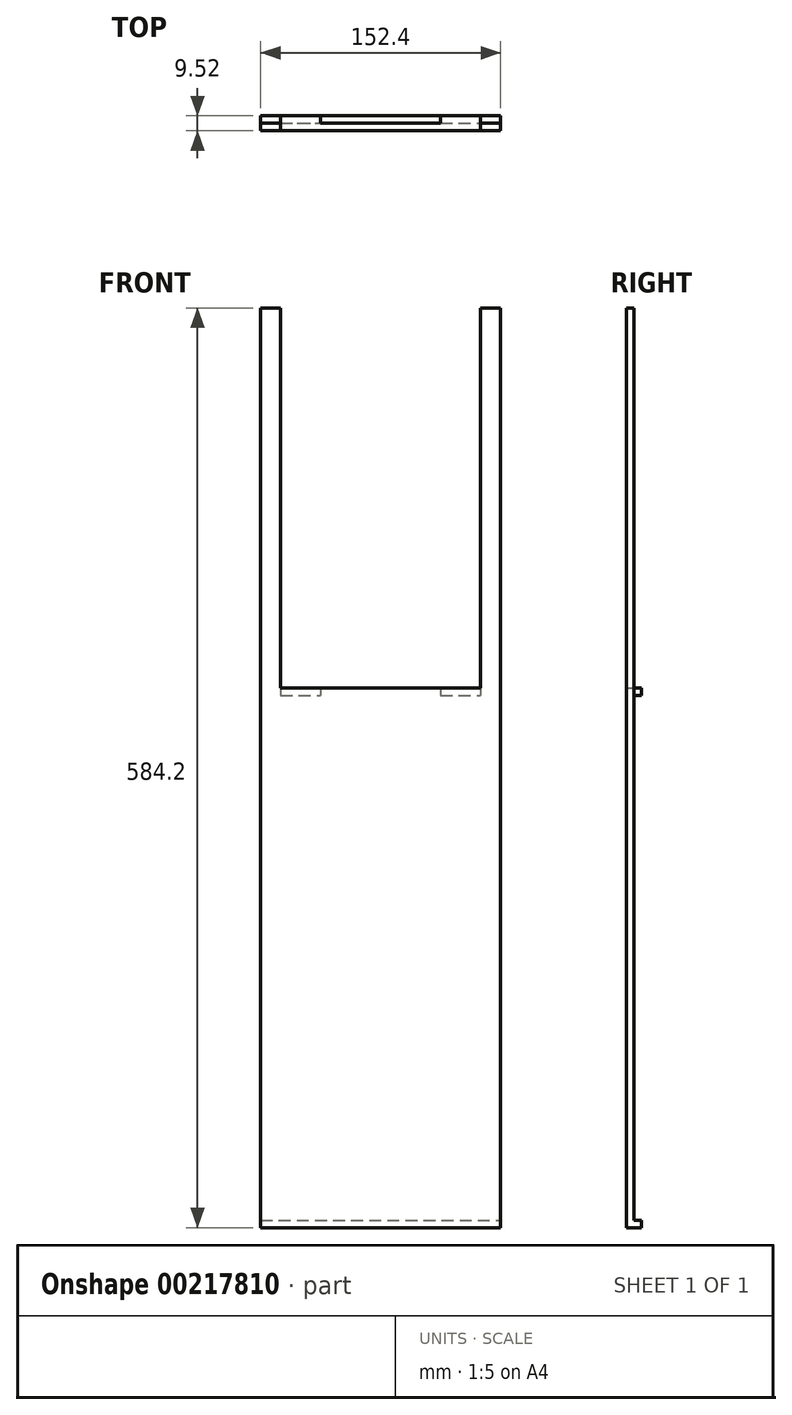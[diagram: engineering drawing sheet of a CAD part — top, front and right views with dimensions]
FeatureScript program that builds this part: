
annotation { "Feature Type Name" : "Feature", "Feature Type Description" : "" }
export const myFeature = defineFeature(function(context is Context, id is Id, definition is map)
    precondition{}
    {
        {
            var Q0;
            Q0=qCreatedBy(makeId("Front.planeOp"),FACE);
            var sketch = newSketch(context, id + "F0", { "sketchPlane" : qUnion([Q0])});
            skLineSegment(sketch, "E0.bottom", {"start": v(76.2, -171.45) * mm, "end": v(-76.2, -171.45) * mm});
            skLineSegment(sketch, "E0.top", {"start": v(76.2, 171.45) * mm, "end": v(-76.2, 171.45) * mm});
            skLineSegment(sketch, "E0.left", {"start": v(76.2, -171.45) * mm, "end": v(76.2, 171.45) * mm});
            skLineSegment(sketch, "E0.right", {"start": v(-76.2, -171.45) * mm, "end": v(-76.2, 171.45) * mm});
            skPoint(sketch, "E0.middle", {"position": v(0, 0) * mm});
            skSolve(sketch);
        }
        {
            var Q0;
            Q0=qSketchRegion(id+"F0",true);
            extrude(context, id + "F1", {"entities" : qUnion([Q0]), "depth" : 4.76 * mm});
        }
        {
            var Q0;
            Q0=makeQuery(id+"F1.opExtrude","CAP_FACE",FACE,{"disambiguationData":[OSD([sQuery(id+"F0.wireOp",EDGE,"E0.bottom"),sQuery(id+"F0.wireOp",EDGE,"E0.top"),sQuery(id+"F0.wireOp",EDGE,"E0.left"),sQuery(id+"F0.wireOp",EDGE,"E0.right")])],"isStart":false});
            var sketch = newSketch(context, id + "F2", { "sketchPlane" : qUnion([Q0])});
            skLineSegment(sketch, "E1.bottom", {"start": v(-63.5, 171.45) * mm, "end": v(-38.1, 171.45) * mm});
            skLineSegment(sketch, "E1.top", {"start": v(-63.5, 166.69) * mm, "end": v(-38.1, 166.69) * mm});
            skLineSegment(sketch, "E1.left", {"start": v(-63.5, 171.45) * mm, "end": v(-63.5, 166.69) * mm});
            skLineSegment(sketch, "E1.right", {"start": v(-38.1, 171.45) * mm, "end": v(-38.1, 166.69) * mm});
            skLineSegment(sketch, "E2.bottom", {"start": v(38.1, 171.45) * mm, "end": v(63.5, 171.45) * mm});
            skLineSegment(sketch, "E2.top", {"start": v(38.1, 166.69) * mm, "end": v(63.5, 166.69) * mm});
            skLineSegment(sketch, "E2.left", {"start": v(38.1, 171.45) * mm, "end": v(38.1, 166.69) * mm});
            skLineSegment(sketch, "E2.right", {"start": v(63.5, 171.45) * mm, "end": v(63.5, 166.69) * mm});
            skSolve(sketch);
        }
        {
            var Q0;
            Q0=qSketchRegion(id+"F2",true);
            extrude(context, id + "F3", {"entities" : qUnion([Q0]), "operationType" : NewBodyOperationType.ADD, "oppositeDirection" : true, "depth" : 9.52 * mm});
        }
        {
            var Q0;
            Q0=makeQuery(id+"F1.opExtrude","CAP_FACE",FACE,{"disambiguationData":[OSD([sQuery(id+"F0.wireOp",EDGE,"E0.bottom"),sQuery(id+"F0.wireOp",EDGE,"E0.top"),sQuery(id+"F0.wireOp",EDGE,"E0.left"),sQuery(id+"F0.wireOp",EDGE,"E0.right")])],"isStart":false});
            var sketch = newSketch(context, id + "F4", { "sketchPlane" : qUnion([Q0])});
            skLineSegment(sketch, "E3.bottom", {"start": v(-76.2, -171.45) * mm, "end": v(76.2, -171.45) * mm});
            skLineSegment(sketch, "E3.top", {"start": v(-76.2, -166.69) * mm, "end": v(76.2, -166.69) * mm});
            skLineSegment(sketch, "E3.left", {"start": v(-76.2, -171.45) * mm, "end": v(-76.2, -166.69) * mm});
            skLineSegment(sketch, "E3.right", {"start": v(76.2, -171.45) * mm, "end": v(76.2, -166.69) * mm});
            skSolve(sketch);
        }
        {
            var Q0;
            Q0=qSketchRegion(id+"F4",true);
            extrude(context, id + "F5", {"entities" : qUnion([Q0]), "operationType" : NewBodyOperationType.ADD, "oppositeDirection" : true, "depth" : 9.52 * mm});
        }
        {
            var Q0;
            Q0=qCreatedBy(makeId("Front.planeOp"),FACE);
            var sketch = newSketch(context, id + "F6", { "sketchPlane" : qUnion([Q0])});
            skLineSegment(sketch, "E4.0", {"start": v(76.2, 171.45) * mm, "end": v(-76.2, 171.45) * mm});
            skLineSegment(sketch, "E5.bottom", {"start": v(-76.2, 171.45) * mm, "end": v(-63.5, 171.45) * mm});
            skLineSegment(sketch, "E5.top", {"start": v(-76.2, 412.75) * mm, "end": v(-63.5, 412.75) * mm});
            skLineSegment(sketch, "E5.left", {"start": v(-76.2, 171.45) * mm, "end": v(-76.2, 412.75) * mm});
            skLineSegment(sketch, "E5.right", {"start": v(-63.5, 171.45) * mm, "end": v(-63.5, 412.75) * mm});
            skLineSegment(sketch, "E6.bottom", {"start": v(76.2, 171.45) * mm, "end": v(63.5, 171.45) * mm});
            skLineSegment(sketch, "E6.top", {"start": v(76.2, 412.75) * mm, "end": v(63.5, 412.75) * mm});
            skLineSegment(sketch, "E6.left", {"start": v(76.2, 171.45) * mm, "end": v(76.2, 412.75) * mm});
            skLineSegment(sketch, "E6.right", {"start": v(63.5, 171.45) * mm, "end": v(63.5, 412.75) * mm});
            skSolve(sketch);
        }
        {
            var Q0;
            Q0 = qSketchRegion(id + "F6", true);
            extrude(context, id + "F7", {"entities" : qUnion([Q0]), "operationType" : NewBodyOperationType.ADD, "depth" : 4.76 * mm});
        }
    });
